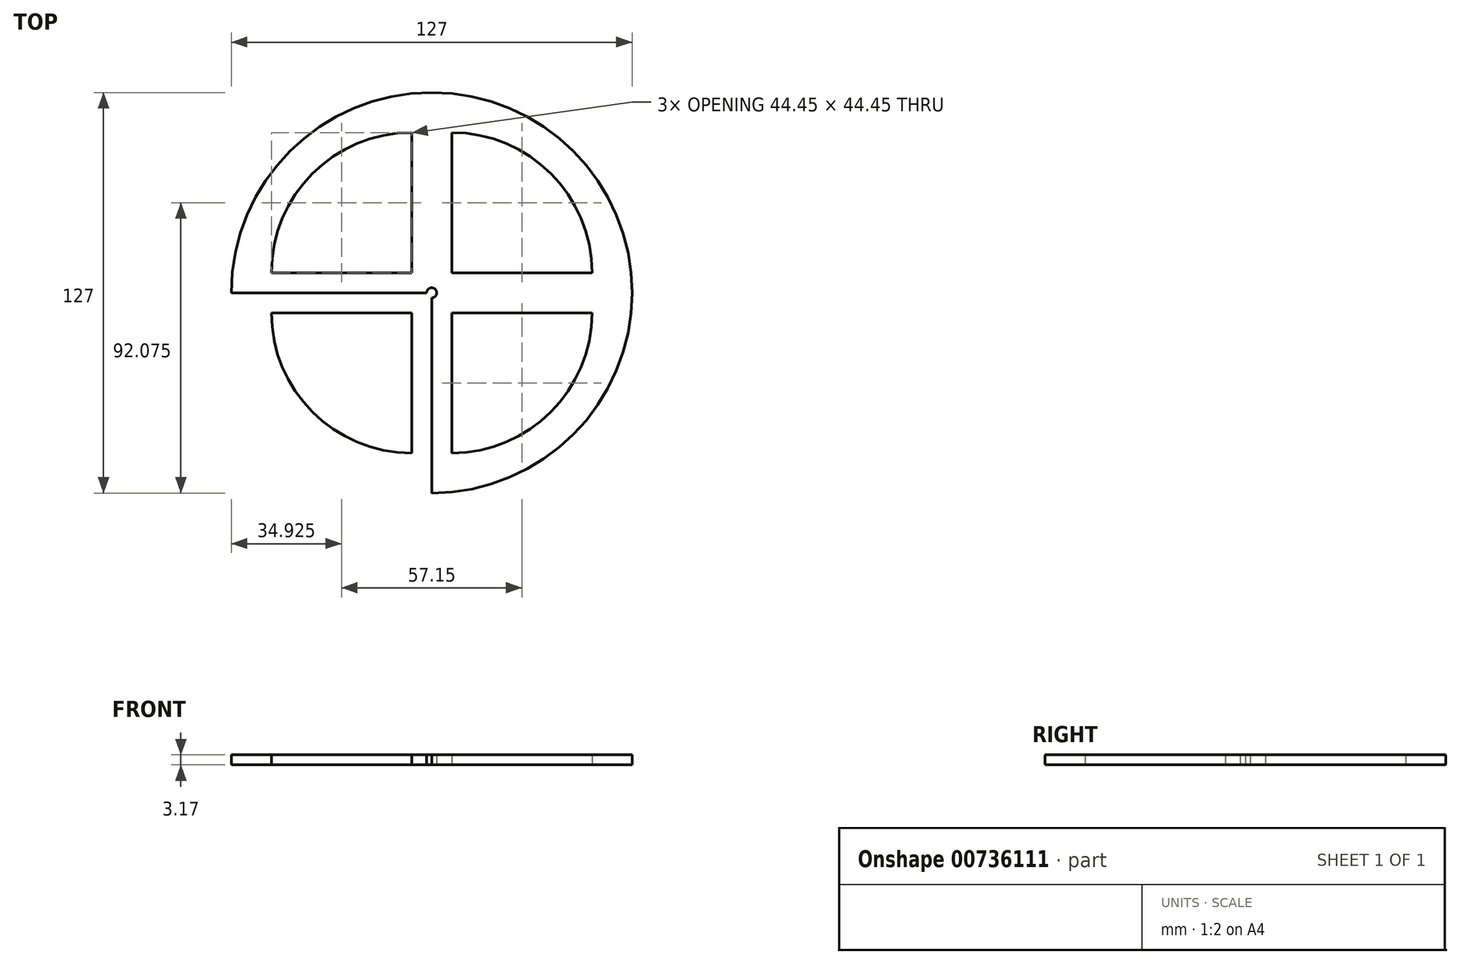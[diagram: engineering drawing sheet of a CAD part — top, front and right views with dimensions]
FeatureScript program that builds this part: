
annotation { "Feature Type Name" : "Feature", "Feature Type Description" : "" }
export const myFeature = defineFeature(function(context is Context, id is Id, definition is map)
    precondition{}
    {
        {
            var Q0;
            Q0=qCreatedBy(makeId("Top.planeOp"),FACE);
            var sketch = newSketch(context, id + "F0", { "sketchPlane" : qUnion([Q0])});
            skCircle(sketch, "E0", {"center": v(0, 0) * mm, "radius": 63.5 * mm});
            skCircle(sketch, "E1", {"center": v(0, 0) * mm, "radius": 1.59 * mm});
            skLineSegment(sketch, "E2", {"start": v(0, 0) * mm, "end": v(0, 63.5) * mm});
            skLineSegment(sketch, "E3", {"start": v(0, 63.5) * mm, "end": v(0, 0) * mm});
            skLineSegment(sketch, "E4", {"start": v(0, -63.5) * mm, "end": v(0, 0) * mm});
            skPoint(sketch, "E5", {"position": v(-6.35, 0) * mm});
            skPoint(sketch, "E6", {"position": v(-6.35, -6.35) * mm});
            skPoint(sketch, "E7", {"position": v(-6.35, -50.8) * mm});
            skArc(sketch, "E8", {"start": v(-6.35, -50.8) * mm, "mid": v(-37.78, -37.78) * mm, "end": v(-50.8, -6.35) * mm});
            skLineSegment(sketch, "E9", {"start": v(-50.8, -6.35) * mm, "end": v(-6.35, -6.35) * mm});
            skLineSegment(sketch, "E10", {"start": v(-6.35, -50.8) * mm, "end": v(-6.35, -6.35) * mm});
            skLineSegment(sketch, "E11", {"start": v(-63.5, 0) * mm, "end": v(63.5, 0) * mm});
            skLineSegment(sketch, "E12.MirrorCS", {"start": v(-50.8, 6.35) * mm, "end": v(-6.35, 6.35) * mm});
            skArc(sketch, "E13.MirrorCS", {"start": v(-6.35, 50.8) * mm, "mid": v(-37.78, 37.78) * mm, "end": v(-50.8, 6.35) * mm});
            skLineSegment(sketch, "E14.MirrorCS", {"start": v(-6.35, 50.8) * mm, "end": v(-6.35, 6.35) * mm});
            skLineSegment(sketch, "E15.MirrorCS", {"start": v(6.35, 50.8) * mm, "end": v(6.35, 6.35) * mm});
            skArc(sketch, "E16.MirrorCS", {"start": v(6.35, 50.8) * mm, "mid": v(37.78, 37.78) * mm, "end": v(50.8, 6.35) * mm});
            skLineSegment(sketch, "E17.MirrorCS", {"start": v(50.8, 6.35) * mm, "end": v(6.35, 6.35) * mm});
            skLineSegment(sketch, "E18.MirrorCS", {"start": v(50.8, -6.35) * mm, "end": v(6.35, -6.35) * mm});
            skArc(sketch, "E19.MirrorCS", {"start": v(6.35, -50.8) * mm, "mid": v(37.78, -37.78) * mm, "end": v(50.8, -6.35) * mm});
            skLineSegment(sketch, "E20.MirrorCS", {"start": v(6.35, -50.8) * mm, "end": v(6.35, -6.35) * mm});
            skSolve(sketch);
        }
        {
            var Q0;
            Q0=makeQuery(id+"F0.imprint","IMPRINT",FACE,{"disambiguationData":[TD([[makeQuery(id+"F0.imprint","IMPRINT",EDGE,{"derivedFrom":sQuery(id+"F0.wireOp",EDGE,"E18.MirrorCS")}),-1.0]])]});
            var Q1;
            Q1=makeQuery(id+"F0.imprint","IMPRINT",FACE,{"disambiguationData":[TD([[makeQuery(id+"F0.imprint","IMPRINT",EDGE,{"derivedFrom":sQuery(id+"F0.wireOp",EDGE,"E15.MirrorCS")}),-1.0]])]});
            var Q2;
            Q2=makeQuery(id+"F0.imprint","IMPRINT",FACE,{"disambiguationData":[TD([[makeQuery(id+"F0.imprint","IMPRINT",EDGE,{"derivedFrom":sQuery(id+"F0.wireOp",EDGE,"E12.MirrorCS")}),-1.0]])]});
            var Q3;
            Q3=makeQuery(id+"F0.imprint","IMPRINT",FACE,{"disambiguationData":[TD([[makeQuery(id+"F0.imprint","IMPRINT",EDGE,{"derivedFrom":sQuery(id+"F0.wireOp",EDGE,"E8")}),1.0]])]});
            extrude(context, id + "F1", {"entities" : qUnion([Q0, Q1, Q2, Q3]), "depth" : 3.17 * mm, "offsetDistance" : 25.4 * mm});
        }
    });
